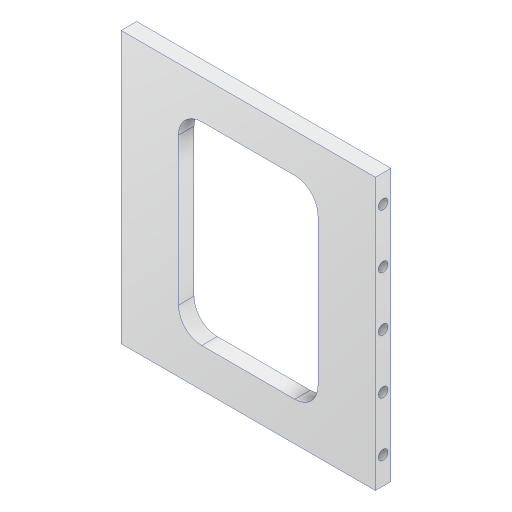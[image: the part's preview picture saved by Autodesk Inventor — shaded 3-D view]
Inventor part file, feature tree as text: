
AUTODESK INVENTOR PART (.ipt)
format: ipt  version: 2023.2 (Build 272271000, 271)  size: 152,576 bytes
history: native  units: mm
features: extrude x3, sketch x3, other x1, mirror x1, fillet x1, projected_geometry x1
ambient origin geometry x8: Origin, YZ Plane, XZ Plane, XY Plane, X Axis, Y Axis, Z Axis, Center Point
bodies: Body1 (feature_tree)
feature tree (10):
  other  "솔리드1"
  extrude  "돌출1"  Depth=65.6mm
  extrude  "돌출2"  Depth=70.0mm
  mirror  "미러1"
  extrude  "돌출3"  Depth=4.0mm TaperAngle=0.0deg
  fillet  "모깎기1"  Radius=2.5mm
  sketch  "스케치1"
  sketch  "스케치2"
  projected_geometry  "투영된 루프1"
  sketch  "스케치3"
